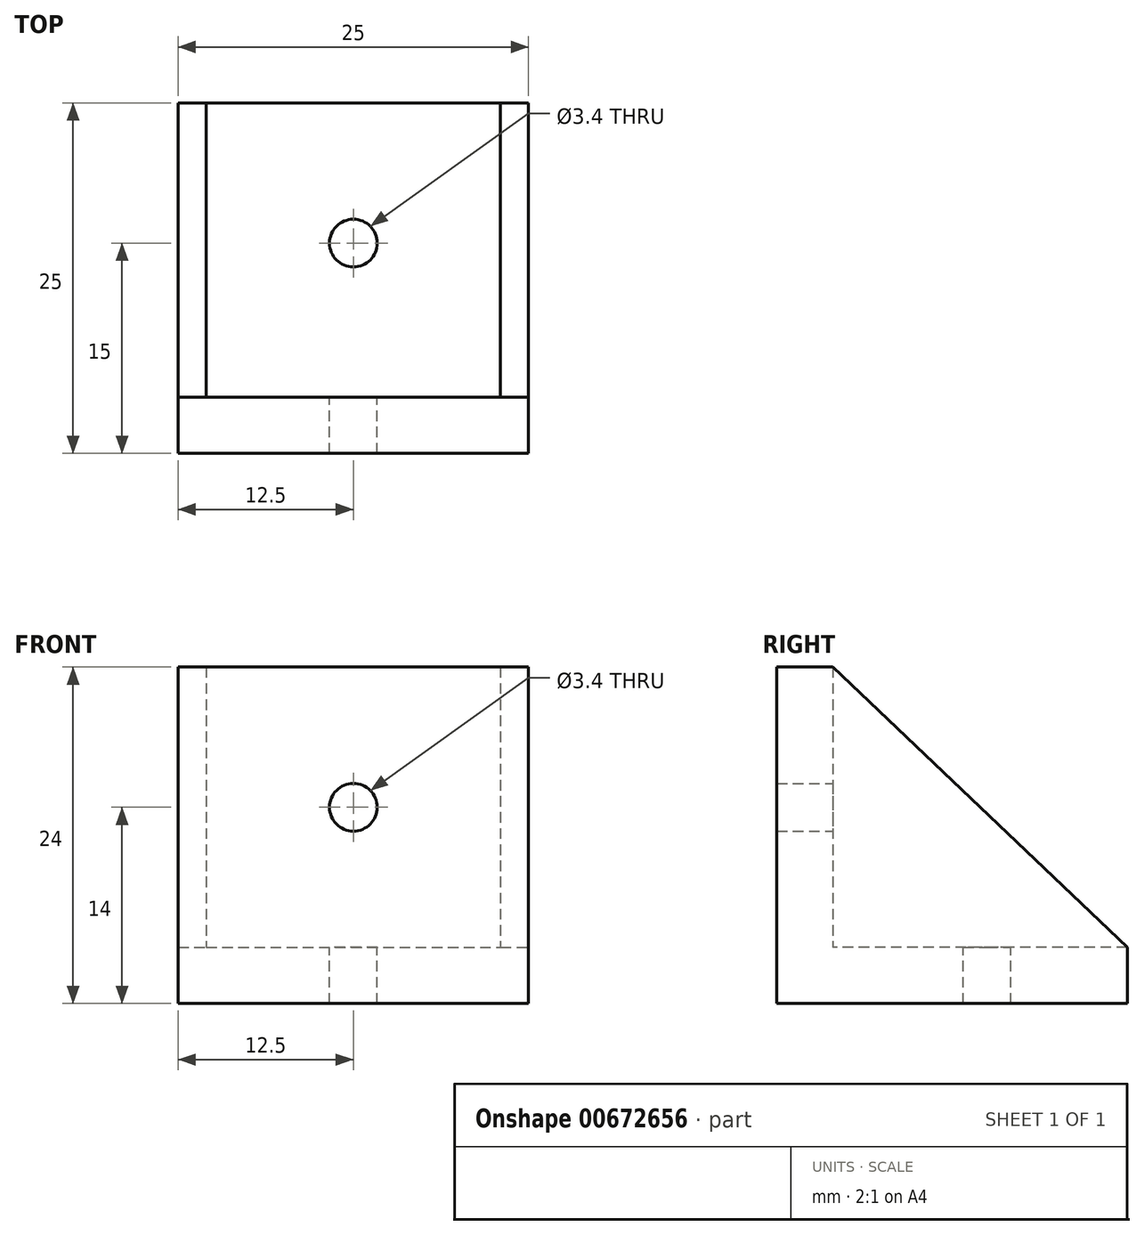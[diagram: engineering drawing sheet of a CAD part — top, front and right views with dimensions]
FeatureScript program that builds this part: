
annotation { "Feature Type Name" : "Feature", "Feature Type Description" : "" }
export const myFeature = defineFeature(function(context is Context, id is Id, definition is map)
    precondition{}
    {
        {
            var Q0;
            Q0=qCreatedBy(makeId("Top.planeOp"),FACE);
            var sketch = newSketch(context, id + "F0", { "sketchPlane" : qUnion([Q0])});
            skLineSegment(sketch, "E0.bottom", {"start": v(0, 0) * mm, "end": v(25, 0) * mm});
            skLineSegment(sketch, "E0.top", {"start": v(0, 25) * mm, "end": v(25, 25) * mm});
            skLineSegment(sketch, "E0.left", {"start": v(0, 0) * mm, "end": v(0, 25) * mm});
            skLineSegment(sketch, "E0.right", {"start": v(25, 0) * mm, "end": v(25, 25) * mm});
            skSolve(sketch);
        }
        {
            var Q0;
            Q0 = qSketchRegion(id + "F0", true);
            extrude(context, id + "F1", {"entities" : qUnion([Q0]), "depth" : 4 * mm, "offsetDistance" : 25 * mm});
        }
        {
            var Q0;
            Q0=makeQuery(id+"F1.opExtrude","CAP_FACE",FACE,{"disambiguationData":[OSD([sQuery(id+"F0.wireOp",EDGE,"E0.bottom"),sQuery(id+"F0.wireOp",EDGE,"E0.top"),sQuery(id+"F0.wireOp",EDGE,"E0.left"),sQuery(id+"F0.wireOp",EDGE,"E0.right")])],"isStart":false});
            var sketch = newSketch(context, id + "F2", { "sketchPlane" : qUnion([Q0])});
            skLineSegment(sketch, "E1.bottom", {"start": v(0, 0) * mm, "end": v(25, 0) * mm});
            skLineSegment(sketch, "E1.top", {"start": v(0, 4) * mm, "end": v(25, 4) * mm});
            skLineSegment(sketch, "E1.left", {"start": v(0, 0) * mm, "end": v(0, 4) * mm});
            skLineSegment(sketch, "E1.right", {"start": v(25, 0) * mm, "end": v(25, 4) * mm});
            skSolve(sketch);
        }
        {
            var Q0;
            Q0 = qSketchRegion(id + "F2", true);
            extrude(context, id + "F3", {"entities" : qUnion([Q0]), "operationType" : NewBodyOperationType.ADD, "depth" : 20 * mm, "offsetDistance" : 25 * mm});
        }
        {
            var Q0;
            Q0=makeQuery(id+"F3.opExtrude","SWEPT_FACE",FACE,{"disambiguationData":[OSD([sQuery(id+"F2.wireOp",EDGE,"E1.top")])]});
            var sketch = newSketch(context, id + "F4", { "sketchPlane" : qUnion([Q0])});
            skLineSegment(sketch, "E2.bottom", {"start": v(-25, 24) * mm, "end": v(-23, 24) * mm});
            skLineSegment(sketch, "E2.top", {"start": v(-25, 4) * mm, "end": v(-23, 4) * mm});
            skLineSegment(sketch, "E2.left", {"start": v(-25, 24) * mm, "end": v(-25, 4) * mm});
            skLineSegment(sketch, "E2.right", {"start": v(-23, 24) * mm, "end": v(-23, 4) * mm});
            skLineSegment(sketch, "E3.bottom", {"start": v(0, 24) * mm, "end": v(-2, 24) * mm});
            skLineSegment(sketch, "E3.top", {"start": v(0, 4) * mm, "end": v(-2, 4) * mm});
            skLineSegment(sketch, "E3.left", {"start": v(0, 24) * mm, "end": v(0, 4) * mm});
            skLineSegment(sketch, "E3.right", {"start": v(-2, 24) * mm, "end": v(-2, 4) * mm});
            skSolve(sketch);
        }
        {
            var Q0;
            Q0 = qSketchRegion(id + "F4", true);
            extrude(context, id + "F5", {"entities" : qUnion([Q0]), "operationType" : NewBodyOperationType.ADD, "depth" : 21 * mm, "offsetDistance" : 25 * mm});
        }
        {
            var Q0;
            Q0=makeQuery(id+"F5.opExtrude","CAP_EDGE",EDGE,{"disambiguationData":[OSD([sQuery(id+"F4.wireOp",EDGE,"E2.bottom")])],"isStart":false});
            var Q1;
            Q1=makeQuery(id+"F5.opExtrude","CAP_EDGE",EDGE,{"disambiguationData":[OSD([sQuery(id+"F4.wireOp",EDGE,"E3.bottom")])],"isStart":false});
            chamfer(context, id + "F6", {"entities" : qUnion([Q0, Q1]), "chamferType" : ChamferType.TWO_OFFSETS, "width1" : 20 * mm, "oppositeDirection" : false, "width2" : 21 * mm, "tangentPropagation" : true});
        }
        {
            var Q0;
            Q0=makeQuery(id+"F3.opExtrude","SWEPT_FACE",FACE,{"disambiguationData":[OSD([sQuery(id+"F2.wireOp",EDGE,"E1.top")])]});
            var sketch = newSketch(context, id + "F7", { "sketchPlane" : qUnion([Q0])});
            skCircle(sketch, "E4", {"center": v(-12.5, 14) * mm, "radius": 1.7 * mm});
            skPoint(sketch, "E4.centerSnap0", {"position": v(-12.5, 24) * mm});
            skSolve(sketch);
        }
        {
            var Q0;
            Q0 = qSketchRegion(id + "F7", true);
            extrude(context, id + "F8", {"entities" : qUnion([Q0]), "operationType" : NewBodyOperationType.REMOVE, "oppositeDirection" : true, "depth" : 25 * mm, "offsetDistance" : 25 * mm});
        }
        {
            var Q0;
            Q0=makeQuery(id+"F1.opExtrude","CAP_FACE",FACE,{"disambiguationData":[OSD([sQuery(id+"F0.wireOp",EDGE,"E0.bottom"),sQuery(id+"F0.wireOp",EDGE,"E0.top"),sQuery(id+"F0.wireOp",EDGE,"E0.left"),sQuery(id+"F0.wireOp",EDGE,"E0.right")])],"isStart":false});
            var sketch = newSketch(context, id + "F9", { "sketchPlane" : qUnion([Q0])});
            skCircle(sketch, "E5", {"center": v(12.5, 15) * mm, "radius": 1.7 * mm});
            skPoint(sketch, "E5.centerSnap0", {"position": v(12.5, 25) * mm});
            skSolve(sketch);
        }
        {
            var Q0;
            Q0 = qSketchRegion(id + "F9", true);
            extrude(context, id + "F10", {"entities" : qUnion([Q0]), "operationType" : NewBodyOperationType.REMOVE, "oppositeDirection" : true, "depth" : 25 * mm, "offsetDistance" : 25 * mm});
        }
    });
